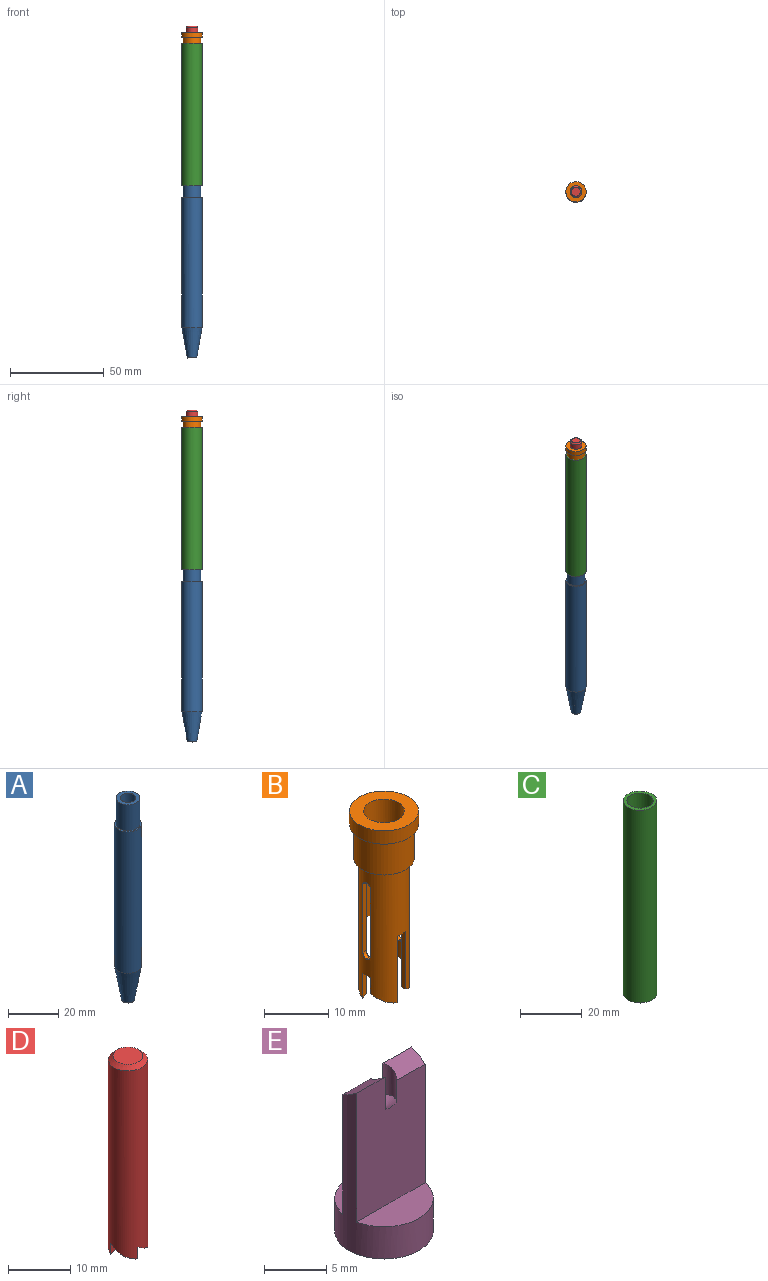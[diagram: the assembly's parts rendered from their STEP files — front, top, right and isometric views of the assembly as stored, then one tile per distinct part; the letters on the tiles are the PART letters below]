
ASSEMBLY  parts=5 mates=4
PART A: 9 faces, bbox 10.8x10.8x98.4 mm
  f0: cylinder r=5.4mm len=69.22mm, axis (0,0,-1), area 2347.3mm2, adj f4,f8
  f1: cylinder r=1.35mm len=5.25mm, axis (0,0,-1), area 44.4mm2, adj f3,f6
  f2: plane 9.53x9.53mm, normal (0,0,1), area 39.6mm2, adj f5,f7
  f3: plane 5.08x5.08mm, normal (0,0,-1), area 14.6mm2, adj f1,f8
  f4: plane 10.8x10.8mm, normal (0,0,1), area 20.3mm2, adj f0,f5
  f5: cylinder r=4.76mm len=12.7mm, axis (0,0,-1), area 380mm2, adj f2,f4
  f6: cone r=0mm half-angle=59deg, axis (0,0,1), area 30.3mm2, adj f1,f7
  f7: cylinder r=3.17mm len=92.08mm, axis (0,0,1), area 1836.8mm2, adj f2,f6
  f8: cone r=2.54mm half-angle=9.8deg, axis (0,0,1), area 417.9mm2, adj f0,f3
PART B: 39 faces, bbox 10.8x10.8x34.3 mm
  f0: cylinder r=3.94mm len=25.4mm, axis (0,0,1), area 510.9mm2, adj f2,f3,f4,f5,f6,f7,f9,f13
  f1: cylinder r=3.17mm len=33.84mm, axis (0,0,-1), area 565.8mm2, adj f2,f3,f4,f5,f6,f7,f11,f13
  f2: plane 10.95x0.78mm, normal (-1,0,0), area 8.6mm2, adj f0,f1,f13,f22
  f3: plane 4.76x0.78mm, normal (0,1,0), area 3.6mm2, adj f0,f1,f17,f22
  f4: plane 10.95x0.78mm, normal (1,0,0), area 8.6mm2, adj f0,f1,f15,f21
  f5: plane 4.76x0.78mm, normal (0,-1,0), area 3.6mm2, adj f0,f1,f16,f21
  f6: plane 12.7x0.78mm, normal (1,0,0), area 9.8mm2, adj f0,f1,f13,f20
  f7: plane 3.01x0.78mm, normal (0,1,0), area 2.4mm2, adj f0,f1,f16,f20
  f8: cylinder r=4.76mm len=9.53mm, axis (0,0,-1), area 190mm2, adj f9,f12
  f9: plane 9.53x9.53mm, normal (0,0,-1), area 22.6mm2, adj f0,f8
  f10: cylinder r=5.4mm len=10.8mm, axis (0,0,-1), area 86.1mm2, adj f11,f12
  f11: plane 10.8x10.8mm, normal (0,0,1), area 59.9mm2, adj f1,f10
  f12: plane 10.8x10.8mm, normal (0,0,-1), area 20.3mm2, adj f8,f10
  f13: plane 1.63x0.87mm, normal (0,0,-1), area 1.2mm2, adj f0,f1,f2,f6
  f14: plane 12.7x0.78mm, normal (-1,0,0), area 9.8mm2, adj f0,f1,f15,f19
  f15: plane 1.63x0.87mm, normal (0,0,-1), area 1.2mm2, adj f0,f1,f4,f14
  f16: plane 1.63x0.87mm, normal (0,0,-1), area 1.2mm2, adj f0,f1,f5,f7
  f17: plane 1.63x0.87mm, normal (0,0,-1), area 1.2mm2, adj f0,f1,f3,f18
  f18: plane 3.01x0.78mm, normal (0,-1,0), area 2.4mm2, adj f0,f1,f17,f19
  f19: plane 3.04x3.04mm, normal (0,-0.5,-0.87), area 3.5mm2, adj f0,f1,f14,f18
  f20: plane 3.04x3.04mm, normal (0,0.5,-0.87), area 3.5mm2, adj f0,f1,f6,f7
  f21: plane 3.04x3.04mm, normal (0.5,0,-0.87), area 3.5mm2, adj f0,f1,f4,f5
  f22: plane 3.04x3.04mm, normal (-0.5,0,-0.87), area 3.5mm2, adj f0,f1,f2,f3
  f23: cylinder r=0.81mm len=0.87mm, axis (-1,0,0), area 1mm2, adj f0,f1,f24,f30
  f24: plane 0.76x0.03mm, normal (0,0,-1), area 0mm2, adj f0,f1,f23,f25
  f25: cylinder r=0.81mm len=0.87mm, axis (-1,0,0), area 1mm2, adj f0,f1,f24,f26
  f26: plane 12.98x0.78mm, normal (0,-1,0), area 10.2mm2, adj f0,f1,f25,f27
  f27: cylinder r=0.81mm len=0.87mm, axis (-1,0,0), area 1mm2, adj f0,f1,f26,f28
  f28: plane 0.76x0.03mm, normal (0,0,1), area 0mm2, adj f0,f1,f27,f29
  f29: cylinder r=0.81mm len=0.87mm, axis (-1,0,0), area 1mm2, adj f0,f1,f28,f30
  f30: plane 12.98x0.78mm, normal (0,1,0), area 10.2mm2, adj f0,f1,f23,f29
  f31: plane 12.98x0.78mm, normal (0,1,0), area 10.2mm2, adj f0,f1,f32,f38
  f32: cylinder r=0.81mm len=0.87mm, axis (-1,0,0), area 1mm2, adj f0,f1,f31,f33
  f33: plane 0.76x0.03mm, normal (0,0,1), area 0mm2, adj f0,f1,f32,f34
  f34: cylinder r=0.81mm len=0.87mm, axis (-1,0,0), area 1mm2, adj f0,f1,f33,f35
  f35: plane 12.98x0.78mm, normal (0,-1,0), area 10.2mm2, adj f0,f1,f34,f36
  f36: cylinder r=0.81mm len=0.87mm, axis (-1,0,0), area 1mm2, adj f0,f1,f35,f37
  f37: plane 0.76x0.03mm, normal (0,0,-1), area 0mm2, adj f0,f1,f36,f38
  f38: cylinder r=0.81mm len=0.87mm, axis (-1,0,0), area 1mm2, adj f0,f1,f31,f37
PART C: 8 faces, bbox 10.8x10.8x76.2 mm
  f0: cylinder r=3.97mm len=50.5mm, axis (0,0,-1), area 1259.3mm2, adj f4,f6
  f1: cylinder r=5.4mm len=76.2mm, axis (0,0,-1), area 2584.2mm2, adj f2,f3
  f2: plane 10.8x10.8mm, normal (0,0,1), area 35.7mm2, adj f1,f5
  f3: plane 10.8x10.8mm, normal (0,0,-1), area 35.7mm2, adj f1,f7
  f4: cone r=0mm half-angle=59deg, axis (0,0,1), area 7.4mm2, adj f0,f5
  f5: cylinder r=4.22mm len=12.7mm, axis (0,0,1), area 336.5mm2, adj f2,f4
  f6: cone r=0mm half-angle=59deg, axis (0,0,-1), area 7.4mm2, adj f0,f7
  f7: cylinder r=4.22mm len=12.7mm, axis (0,0,-1), area 336.5mm2, adj f3,f6
PART D: 13 faces, bbox 6.4x6.4x38.1 mm
  f0: cylinder r=3.17mm len=37.28mm, axis (0,0,-1), area 724.8mm2, adj f2,f5,f6,f7,f8,f9,f10,f11
  f1: plane 4.83x4.83mm, normal (0,0,1), area 18.3mm2, adj f2
  f2: cone r=2.41mm half-angle=45deg, axis (0,0,-1), area 18.9mm2, adj f0,f1
  f3: cone r=0mm half-angle=59deg, axis (0,0,-1), area 9.2mm2, adj f4
  f4: cylinder r=1.59mm len=24.35mm, axis (0,0,-1), area 237.1mm2, adj f3,f5,f6,f7,f8,f9,f10,f11
  f5: plane 2.24x1.71mm, normal (1,0,0), area 3mm2, adj f0,f4,f6,f9
  f6: plane 3.88x2.36mm, normal (-0.5,0,-0.87), area 6.9mm2, adj f0,f4,f5,f11
  f7: plane 2.24x1.71mm, normal (-1,0,0), area 3mm2, adj f0,f4,f8,f12
  f8: plane 3.88x2.36mm, normal (0.5,0,-0.87), area 6.9mm2, adj f0,f4,f7,f10
  f9: plane 3.9x2.38mm, normal (0,0.5,-0.87), area 6.9mm2, adj f0,f4,f5,f10
  f10: plane 2.24x1.71mm, normal (0,-1,0), area 3mm2, adj f0,f4,f8,f9
  f11: plane 2.24x1.71mm, normal (0,1,0), area 3mm2, adj f0,f4,f6,f12
  f12: plane 3.88x2.36mm, normal (0,-0.5,-0.87), area 6.9mm2, adj f0,f4,f7,f11
PART E: 11 faces, bbox 8x8x15.9 mm
  f0: plane 12.59x7.78mm, normal (0,1,0), area 91.2mm2, adj f3,f4,f6,f7,f8,f9,f10
  f1: plane 12.69x7.78mm, normal (0,-1,0), area 91.2mm2, adj f2,f3,f6,f7,f8,f9,f10
  f2: plane 7.78x3.18mm, normal (0,0,1), area 18.5mm2, adj f1,f3
  f3: cylinder r=3.97mm len=15.87mm, axis (0,0,-1), area 117.8mm2, adj f0,f1,f2,f4,f5,f9,f10
  f4: plane 7.78x3.18mm, normal (0,0,1), area 18.5mm2, adj f0,f3
  f5: plane 7.94x7.94mm, normal (0,0,-1), area 49.5mm2, adj f3
  f6: cone r=0mm half-angle=59deg, axis (0,0,1), area 3.4mm2, adj f0,f1,f7,f8
  f7: cylinder r=1.03mm len=3.07mm, axis (0,0,1), area 4.7mm2, adj f0,f1,f6,f9
  f8: cylinder r=1.03mm len=3.17mm, axis (0,0,1), area 4.9mm2, adj f0,f1,f6,f10
  f9: plane 3.35x1.62mm, normal (0,-0.5,0.87), area 5.5mm2, adj f0,f1,f3,f7
  f10: plane 3.35x1.62mm, normal (0,0.5,0.87), area 5.5mm2, adj f0,f1,f3,f8
PLACE A t=(-0.99,17.23,-103.48)mm
PLACE B t=(-0.99,17.23,61.62)mm
PLACE C t=(-0.99,17.23,-11.4)mm
PLACE D t=(-0.99,17.23,35.92)mm
PLACE E t=(-0.99,17.23,2.36)mm
MATE cylindrical B.f8 <-> C.f1  axis (0,0,-1) through (-0.99,17.23,64.8)mm
MATE cylindrical D.f0 <-> B.f0  axis (0,0,-1) through (-0.99,17.23,54.51)mm
MATE cylindrical A.f5 <-> C.f6  axis (0,0,-1) through (-0.99,17.23,-11.4)mm
MATE cylindrical E.f3 <-> B.f10  axis (0,0,-1) through (-0.99,17.23,2.36)mm
